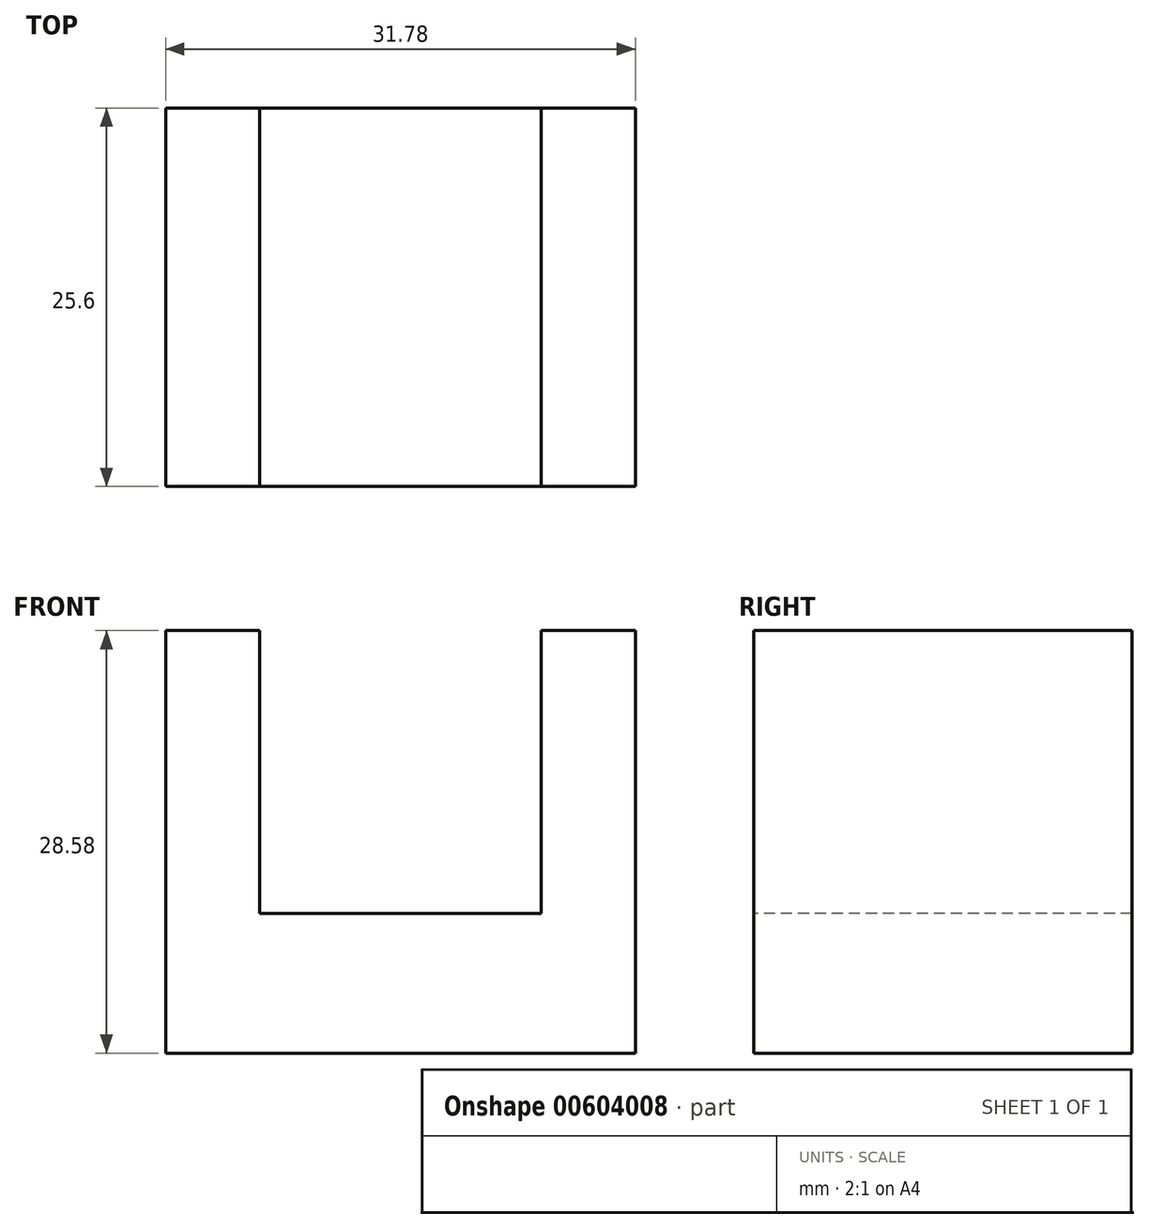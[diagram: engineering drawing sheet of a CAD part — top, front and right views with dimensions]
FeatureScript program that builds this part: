
annotation { "Feature Type Name" : "Feature", "Feature Type Description" : "" }
export const myFeature = defineFeature(function(context is Context, id is Id, definition is map)
    precondition{}
    {
        {
            var Q0;
            Q0=qCreatedBy(makeId("Top.planeOp"),FACE);
            var sketch = newSketch(context, id + "F0", { "sketchPlane" : qUnion([Q0])});
            skLineSegment(sketch, "E0.bottom", {"start": v(15.9, 12.8) * mm, "end": v(-15.89, 12.8) * mm});
            skLineSegment(sketch, "E0.top", {"start": v(15.9, -12.8) * mm, "end": v(-15.9, -12.8) * mm});
            skLineSegment(sketch, "E0.left", {"start": v(15.9, 12.8) * mm, "end": v(15.9, -12.8) * mm});
            skLineSegment(sketch, "E0.right", {"start": v(-15.89, 12.8) * mm, "end": v(-15.9, -12.8) * mm});
            skPoint(sketch, "E0.middle", {"position": v(0, 0) * mm});
            skSolve(sketch);
        }
        {
            var Q0;
            Q0=makeQuery(id+"F0.imprint","IMPRINT",FACE,{"disambiguationData":[TD([[makeQuery(id+"F0.imprint","IMPRINT",EDGE,{"derivedFrom":sQuery(id+"F0.wireOp",EDGE,"E0.bottom")}),1.0]])]});
            extrude(context, id + "F1", {"entities" : qUnion([Q0]), "depth" : 9.46 * mm, "offsetDistance" : 25 * mm});
        }
        {
            var Q0;
            Q0=makeQuery(id+"F1.opExtrude","CAP_FACE",FACE,{"disambiguationData":[OSD([sQuery(id+"F0.wireOp",EDGE,"E0.bottom"),sQuery(id+"F0.wireOp",EDGE,"E0.top"),sQuery(id+"F0.wireOp",EDGE,"E0.left"),sQuery(id+"F0.wireOp",EDGE,"E0.right")])],"isStart":false});
            var sketch = newSketch(context, id + "F2", { "sketchPlane" : qUnion([Q0])});
            skLineSegment(sketch, "E1.bottom", {"start": v(-15.89, 12.8) * mm, "end": v(-9.52, 12.8) * mm});
            skLineSegment(sketch, "E1.top", {"start": v(-15.89, -12.8) * mm, "end": v(-9.52, -12.8) * mm});
            skLineSegment(sketch, "E1.left", {"start": v(-15.89, 12.8) * mm, "end": v(-15.89, -12.8) * mm});
            skLineSegment(sketch, "E1.right", {"start": v(-9.52, 12.8) * mm, "end": v(-9.52, -12.8) * mm});
            skLineSegment(sketch, "E2.bottom", {"start": v(15.9, 12.8) * mm, "end": v(9.52, 12.8) * mm});
            skLineSegment(sketch, "E2.top", {"start": v(15.9, -12.8) * mm, "end": v(9.52, -12.8) * mm});
            skLineSegment(sketch, "E2.left", {"start": v(15.9, 12.8) * mm, "end": v(15.9, -12.8) * mm});
            skLineSegment(sketch, "E2.right", {"start": v(9.52, 12.8) * mm, "end": v(9.52, -12.8) * mm});
            skSolve(sketch);
        }
        {
            var Q0;
            Q0 = qSketchRegion(id + "F2", true);
            extrude(context, id + "F3", {"entities" : qUnion([Q0]), "operationType" : NewBodyOperationType.ADD, "depth" : 19.12 * mm, "offsetDistance" : 25 * mm});
        }
    });
